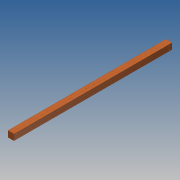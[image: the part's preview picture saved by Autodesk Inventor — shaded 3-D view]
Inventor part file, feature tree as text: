
AUTODESK INVENTOR PART (.ipt)
format: ipt  version: 2014 SP1 (Build 180222100, 222)  size: 97,792 bytes
history: native  units: in
note: dims shown in document units (in); Inventor stores cm internally (conversion verified against a paired STEP export)
features: hole x2, sketch x2, extrude x1
ambient origin geometry x8: Origin, YZ Plane, XZ Plane, XY Plane, X Axis, Y Axis, Z Axis, Center Point
bodies: Solid1 (feature_tree)
feature tree (5):
  extrude  "Extrusion1"  Depth=1.5in
  hole  "Hole2"  [1 undecoded]
  hole  "Hole4"  [1 undecoded]
  sketch  "Sketch1"  dims[d0=1.5in d1=1.5in]
  sketch  "Sketch3"  dims[d2=39.0in d3=0.0in d21=1.0in d22=0.201in d23=0.75in d24=0.385in d25=0.25in d26=0.5635in d27=1.0in d28=0.8108in d29=0.375in d30=0.75in d38=0.201in d39=0.75in d40=0.385in d41=0.25in d42=0.5635in d43=1.0in d44=0.8108in]
note: 2 required parameter values undecoded (feature->parameter linkage not recoverable at this tier; creation-order binding heuristic only, values carry confidence <= 0.55)
